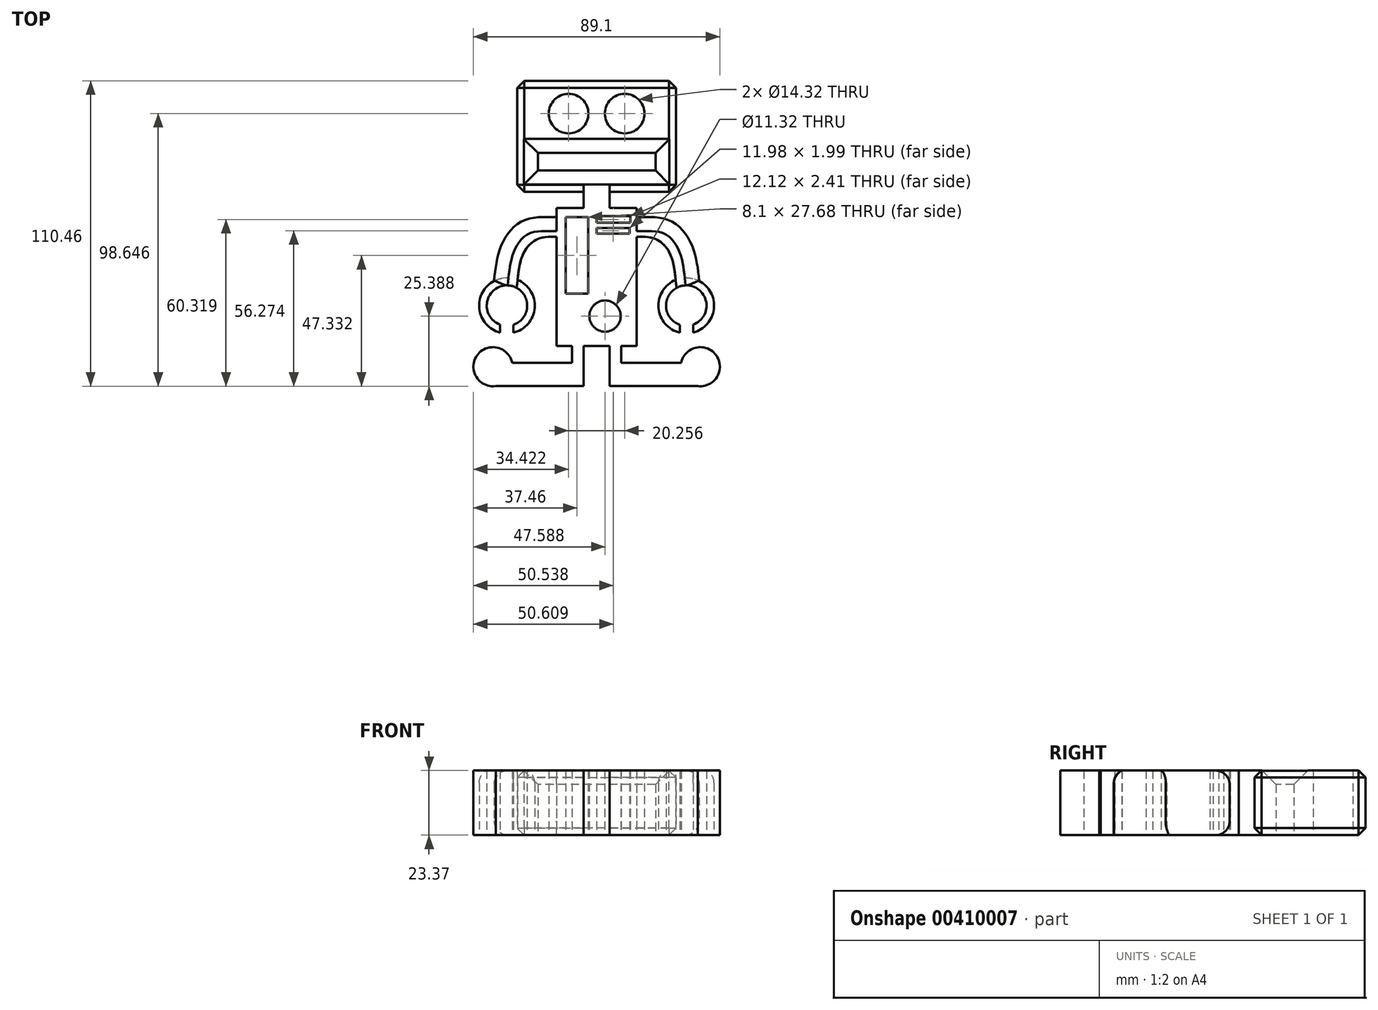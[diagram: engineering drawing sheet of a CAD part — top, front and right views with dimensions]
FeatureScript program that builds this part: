
annotation { "Feature Type Name" : "Feature", "Feature Type Description" : "" }
export const myFeature = defineFeature(function(context is Context, id is Id, definition is map)
    precondition{}
    {
        {
            var Q0;
            Q0=qCreatedBy(makeId("Top.planeOp"),FACE);
            var sketch = newSketch(context, id + "F0", { "sketchPlane" : qUnion([Q0])});
            skLineSegment(sketch, "E0.bottom", {"start": v(-28.7, 40.17) * mm, "end": v(0, 40.17) * mm});
            skLineSegment(sketch, "E0.left", {"start": v(-28.7, 40.17) * mm, "end": v(-28.7, 0) * mm});
            skLineSegment(sketch, "E1.MirrorCS", {"start": v(28.7, 40.17) * mm, "end": v(0, 40.17) * mm});
            skLineSegment(sketch, "E2.MirrorCS", {"start": v(28.7, 40.17) * mm, "end": v(28.7, 0) * mm});
            skCircle(sketch, "E3", {"center": v(-10.13, 28.36) * mm, "radius": 7.16 * mm});
            skLineSegment(sketch, "E4.bottom", {"start": v(-21.27, 14.18) * mm, "end": v(0, 14.18) * mm});
            skLineSegment(sketch, "E4.top", {"start": v(-21.27, 7.76) * mm, "end": v(0, 7.76) * mm});
            skLineSegment(sketch, "E4.left", {"start": v(-21.27, 14.18) * mm, "end": v(-21.27, 7.76) * mm});
            skLineSegment(sketch, "E5.MirrorCS", {"start": v(21.27, 14.18) * mm, "end": v(21.27, 7.76) * mm});
            skLineSegment(sketch, "E6.MirrorCS", {"start": v(21.27, 14.18) * mm, "end": v(0, 14.18) * mm});
            skLineSegment(sketch, "E7.MirrorCS", {"start": v(21.27, 7.76) * mm, "end": v(0, 7.76) * mm});
            skCircle(sketch, "E8.MirrorC", {"center": v(10.13, 28.36) * mm, "radius": 7.16 * mm});
            skLineSegment(sketch, "E9", {"start": v(-4.73, 0) * mm, "end": v(-4.73, -5.74) * mm});
            skLineSegment(sketch, "E10", {"start": v(-4.73, -5.74) * mm, "end": v(-14.52, -5.74) * mm});
            skLineSegment(sketch, "E11", {"start": v(-14.52, -5.74) * mm, "end": v(-14.52, -9.12) * mm});
            skLineSegment(sketch, "E12", {"start": v(-14.52, -55.7) * mm, "end": v(-8.9, -55.7) * mm});
            skFitSpline(sketch, "E13", {"points": [v(-14.52, -9.12) * mm, v(-26.67, -10.47) * mm, v(-34.43, -19.24) * mm, v(-37.14, -32.75) * mm], "startDerivative": vector(-39.34, 1.38) * mm, "endDerivative": vector(-4.09, -40.26) * mm});
            skFitSpline(sketch, "E14", {"points": [v(-14.52, -16.2) * mm, v(-20.93, -16.88) * mm, v(-26.33, -21.95) * mm, v(-28.7, -32.75) * mm], "startDerivative": vector(-22.24, 0.54) * mm, "endDerivative": vector(-3.26, -30.34) * mm});
            skArc(sketch, "E15", {"start": v(-37.08, -32.2) * mm, "mid": v(-42.4, -42.23) * mm, "end": v(-34.98, -50.83) * mm});
            skArc(sketch, "E16", {"start": v(-30.1, -48.04) * mm, "mid": v(-32.28, -33.79) * mm, "end": v(-34.98, -47.95) * mm});
            skLineSegment(sketch, "E17", {"start": v(-34.98, -47.95) * mm, "end": v(-34.98, -50.83) * mm});
            skLineSegment(sketch, "E18", {"start": v(-30.1, -48.04) * mm, "end": v(-30.1, -50.9) * mm});
            skArc(sketch, "E19.trimOffspring", {"start": v(-30.1, -50.9) * mm, "mid": v(-22.38, -41.9) * mm, "end": v(-28.6, -31.8) * mm});
            skLineSegment(sketch, "E20.bottom", {"start": v(-30.55, -61.78) * mm, "end": v(-8.9, -61.78) * mm});
            skLineSegment(sketch, "E20.top", {"start": v(-37.47, -70.22) * mm, "end": v(-4.73, -70.22) * mm});
            skLineSegment(sketch, "E20.right", {"start": v(-4.73, -61.78) * mm, "end": v(-4.73, -70.22) * mm});
            skLineSegment(sketch, "E21.left", {"start": v(-8.9, -55.7) * mm, "end": v(-8.9, -61.78) * mm});
            skLineSegment(sketch, "E21.right", {"start": v(-4.73, -55.7) * mm, "end": v(-4.73, -61.78) * mm});
            skLineSegment(sketch, "E22.trimOffspring", {"start": v(-4.73, -55.7) * mm, "end": v(0, -55.7) * mm});
            skLineSegment(sketch, "E23.trimOffspring", {"start": v(-14.52, -16.2) * mm, "end": v(-14.52, -55.7) * mm});
            skPoint(sketch, "E24.orphan", {"position": v(0, -5.74) * mm});
            skLineSegment(sketch, "E25.MirrorCS", {"start": v(14.52, -5.74) * mm, "end": v(14.52, -9.12) * mm});
            skLineSegment(sketch, "E26.MirrorCS", {"start": v(4.73, -55.7) * mm, "end": v(4.73, -61.78) * mm});
            skLineSegment(sketch, "E27.MirrorCS", {"start": v(30.1, -48.04) * mm, "end": v(30.1, -50.9) * mm});
            skLineSegment(sketch, "E28.MirrorCS", {"start": v(8.9, -55.7) * mm, "end": v(8.9, -61.78) * mm});
            skLineSegment(sketch, "E29.MirrorCS", {"start": v(4.73, -61.78) * mm, "end": v(4.73, -70.22) * mm});
            skLineSegment(sketch, "E30.MirrorCS", {"start": v(34.98, -47.95) * mm, "end": v(34.98, -50.83) * mm});
            skLineSegment(sketch, "E31.MirrorCS", {"start": v(14.52, -55.7) * mm, "end": v(8.9, -55.7) * mm});
            skLineSegment(sketch, "E32.MirrorCS", {"start": v(4.73, -55.7) * mm, "end": v(0, -55.7) * mm});
            skLineSegment(sketch, "E33.MirrorCS", {"start": v(4.73, 0) * mm, "end": v(4.73, -5.74) * mm});
            skFitSpline(sketch, "E34.MirrorCS", {"points": [v(14.52, -16.2) * mm, v(20.93, -16.88) * mm, v(26.33, -21.95) * mm, v(28.7, -32.75) * mm], "startDerivative": vector(22.24, 0.54) * mm, "endDerivative": vector(3.26, -30.34) * mm});
            skArc(sketch, "E35.MirrorCS", {"start": v(30.1, -50.9) * mm, "mid": v(22.38, -41.9) * mm, "end": v(28.6, -31.8) * mm});
            skFitSpline(sketch, "E36.MirrorCS", {"points": [v(14.52, -9.12) * mm, v(26.67, -10.47) * mm, v(34.43, -19.24) * mm, v(37.14, -32.75) * mm], "startDerivative": vector(39.34, 1.38) * mm, "endDerivative": vector(4.09, -40.26) * mm});
            skLineSegment(sketch, "E37.MirrorCS", {"start": v(14.52, -16.2) * mm, "end": v(14.52, -55.7) * mm});
            skArc(sketch, "E38.MirrorCS", {"start": v(37.08, -32.2) * mm, "mid": v(42.4, -42.23) * mm, "end": v(34.98, -50.83) * mm});
            skLineSegment(sketch, "E39.MirrorCS", {"start": v(37.47, -70.22) * mm, "end": v(4.73, -70.22) * mm});
            skArc(sketch, "E40.MirrorCS", {"start": v(30.1, -48.04) * mm, "mid": v(32.28, -33.79) * mm, "end": v(34.98, -47.95) * mm});
            skLineSegment(sketch, "E41.MirrorCS", {"start": v(30.55, -61.78) * mm, "end": v(8.9, -61.78) * mm});
            skLineSegment(sketch, "E42.MirrorCS", {"start": v(4.73, -5.74) * mm, "end": v(14.52, -5.74) * mm});
            skPoint(sketch, "E43.orphan", {"position": v(0, 0) * mm});
            skPoint(sketch, "E44.MirrorCS.start.orphan", {"position": v(28.7, 0) * mm});
            skLineSegment(sketch, "E45", {"start": v(-28.7, 0) * mm, "end": v(-4.73, 0) * mm});
            skLineSegment(sketch, "E46", {"start": v(4.73, 0) * mm, "end": v(28.7, 0) * mm});
            skArc(sketch, "E47", {"start": v(-30.55, -61.78) * mm, "mid": v(-43.25, -59.13) * mm, "end": v(-36.51, -70.22) * mm});
            skPoint(sketch, "E20.left.start.orphan", {"position": v(-37.47, -61.78) * mm});
            skArc(sketch, "E48.MirrorCS", {"start": v(30.55, -61.78) * mm, "mid": v(43.25, -59.13) * mm, "end": v(36.51, -70.22) * mm});
            skPoint(sketch, "E49.MirrorP", {"position": v(37.47, -61.78) * mm});
            skPoint(sketch, "E50.orphan", {"position": v(-37.47, -70.22) * mm});
            skLineSegment(sketch, "E51.bottom", {"start": v(-11.14, -9.12) * mm, "end": v(-3.04, -9.12) * mm});
            skLineSegment(sketch, "E51.top", {"start": v(-11.14, -36.8) * mm, "end": v(-3.04, -36.8) * mm});
            skLineSegment(sketch, "E51.left", {"start": v(-11.14, -9.12) * mm, "end": v(-11.14, -36.8) * mm});
            skLineSegment(sketch, "E51.right", {"start": v(-3.04, -9.12) * mm, "end": v(-3.04, -36.8) * mm});
            skLineSegment(sketch, "E52.bottom", {"start": v(0, -8.76) * mm, "end": v(12.12, -8.76) * mm});
            skLineSegment(sketch, "E52.top", {"start": v(0, -11.18) * mm, "end": v(12.12, -11.18) * mm});
            skLineSegment(sketch, "E52.left", {"start": v(0, -8.76) * mm, "end": v(0, -11.18) * mm});
            skLineSegment(sketch, "E52.right", {"start": v(12.12, -8.76) * mm, "end": v(12.12, -11.18) * mm});
            skLineSegment(sketch, "E53.bottom", {"start": v(0, -13.02) * mm, "end": v(11.98, -13.02) * mm});
            skLineSegment(sketch, "E53.top", {"start": v(0, -15) * mm, "end": v(11.98, -15) * mm});
            skLineSegment(sketch, "E53.left", {"start": v(0, -13.02) * mm, "end": v(0, -15) * mm});
            skLineSegment(sketch, "E53.right", {"start": v(11.98, -13.02) * mm, "end": v(11.98, -15) * mm});
            skCircle(sketch, "E54", {"center": v(3.04, -44.9) * mm, "radius": 5.66 * mm});
            skSolve(sketch);
        }
        {
            var Q0;
            Q0=makeQuery(id+"F0.imprint","IMPRINT",FACE,{"disambiguationData":[TD([[makeQuery(id+"F0.imprint","IMPRINT",EDGE,{"derivedFrom":sQuery(id+"F0.wireOp",EDGE,"E0.bottom")}),-1.0]])]});
            extrude(context, id + "F1", {"entities" : qUnion([Q0]), "depth" : 23.37 * mm});
        }
        {
            var Q0;
            Q0=makeQuery(id+"F1.opExtrude","CAP_EDGE",EDGE,{"disambiguationData":[OSD([sQuery(id+"F0.wireOp",EDGE,"E13")])],"isStart":false});
            var Q1;
            Q1=makeQuery(id+"F1.opExtrude","CAP_EDGE",EDGE,{"disambiguationData":[OSD([sQuery(id+"F0.wireOp",EDGE,"E36.MirrorCS")])],"isStart":false});
            var Q2;
            Q2=makeQuery(id+"F1.opExtrude","CAP_EDGE",EDGE,{"disambiguationData":[OSD([sQuery(id+"F0.wireOp",EDGE,"E13")])],"isStart":true});
            var Q3;
            Q3=makeQuery(id+"F1.opExtrude","CAP_EDGE",EDGE,{"disambiguationData":[OSD([sQuery(id+"F0.wireOp",EDGE,"E36.MirrorCS")])],"isStart":true});
            fillet(context, id + "F2", {"entities" : qUnion([Q0, Q1, Q2, Q3]), "radius" : 5.08 * mm, "tangentPropagation" : true, "allowEdgeOverflow" : false});
        }
        {
            var Q0;
            Q0=makeQuery(id+"F1.opExtrude","SWEPT_EDGE",EDGE,{"disambiguationData":[OSD([sQuery(id+"F0.wireOp",EDGE,"E0.bottom"),sQuery(id+"F0.wireOp",EDGE,"E0.left")])]});
            var Q1;
            Q1=makeQuery(id+"F1.opExtrude","CAP_EDGE",EDGE,{"disambiguationData":[OSD([sQuery(id+"F0.wireOp",EDGE,"E0.left")])],"isStart":false});
            var Q2;
            Q2=makeQuery(id+"F1.opExtrude","CAP_EDGE",EDGE,{"disambiguationData":[OSD([sQuery(id+"F0.wireOp",EDGE,"E0.bottom"),sQuery(id+"F0.wireOp",EDGE,"E1.MirrorCS")])],"isStart":false});
            var Q3;
            Q3=makeQuery(id+"F1.opExtrude","CAP_EDGE",EDGE,{"disambiguationData":[OSD([sQuery(id+"F0.wireOp",EDGE,"E2.MirrorCS")])],"isStart":false});
            var Q4;
            Q4=makeQuery(id+"F1.opExtrude","CAP_EDGE",EDGE,{"disambiguationData":[OSD([sQuery(id+"F0.wireOp",EDGE,"E46")])],"isStart":false});
            var Q5;
            Q5=makeQuery(id+"F1.opExtrude","CAP_EDGE",EDGE,{"disambiguationData":[OSD([sQuery(id+"F0.wireOp",EDGE,"E45")])],"isStart":false});
            var Q6;
            Q6=makeQuery(id+"F1.opExtrude","SWEPT_EDGE",EDGE,{"disambiguationData":[OSD([sQuery(id+"F0.wireOp",EDGE,"E2.MirrorCS"),sQuery(id+"F0.wireOp",EDGE,"E46")])]});
            var Q7;
            Q7=makeQuery(id+"F1.opExtrude","CAP_EDGE",EDGE,{"disambiguationData":[OSD([sQuery(id+"F0.wireOp",EDGE,"E0.bottom"),sQuery(id+"F0.wireOp",EDGE,"E1.MirrorCS")])],"isStart":true});
            var Q8;
            Q8=makeQuery(id+"F1.opExtrude","SWEPT_EDGE",EDGE,{"disambiguationData":[OSD([sQuery(id+"F0.wireOp",EDGE,"E1.MirrorCS"),sQuery(id+"F0.wireOp",EDGE,"E2.MirrorCS")])]});
            var Q9;
            Q9=makeQuery(id+"F1.opExtrude","CAP_EDGE",EDGE,{"disambiguationData":[OSD([sQuery(id+"F0.wireOp",EDGE,"E2.MirrorCS")])],"isStart":true});
            var Q10;
            Q10=makeQuery(id+"F1.opExtrude","CAP_EDGE",EDGE,{"disambiguationData":[OSD([sQuery(id+"F0.wireOp",EDGE,"E46")])],"isStart":true});
            var Q11;
            Q11=makeQuery(id+"F1.opExtrude","CAP_EDGE",EDGE,{"disambiguationData":[OSD([sQuery(id+"F0.wireOp",EDGE,"E45")])],"isStart":true});
            var Q12;
            Q12=makeQuery(id+"F1.opExtrude","CAP_EDGE",EDGE,{"disambiguationData":[OSD([sQuery(id+"F0.wireOp",EDGE,"E0.left")])],"isStart":true});
            var Q13;
            Q13=makeQuery(id+"F1.opExtrude","SWEPT_EDGE",EDGE,{"disambiguationData":[OSD([sQuery(id+"F0.wireOp",EDGE,"E0.left"),sQuery(id+"F0.wireOp",EDGE,"E45")])]});
            chamfer(context, id + "F3", {"entities" : qUnion([Q0, Q1, Q2, Q3, Q4, Q5, Q6, Q7, Q8, Q9, Q10, Q11, Q12, Q13]), "width" : 2.54 * mm, "tangentPropagation" : true});
        }
        {
            var Q0;
            Q0=makeQuery(id+"F1.opExtrude","CAP_EDGE",EDGE,{"disambiguationData":[OSD([sQuery(id+"F0.wireOp",EDGE,"E4.bottom"),sQuery(id+"F0.wireOp",EDGE,"E6.MirrorCS")])],"isStart":false});
            var Q1;
            Q1=makeQuery(id+"F1.opExtrude","CAP_EDGE",EDGE,{"disambiguationData":[OSD([sQuery(id+"F0.wireOp",EDGE,"E4.top"),sQuery(id+"F0.wireOp",EDGE,"E7.MirrorCS")])],"isStart":false});
            var Q2;
            Q2=makeQuery(id+"F1.opExtrude","CAP_EDGE",EDGE,{"disambiguationData":[OSD([sQuery(id+"F0.wireOp",EDGE,"E4.left")])],"isStart":false});
            var Q3;
            Q3=makeQuery(id+"F1.opExtrude","CAP_EDGE",EDGE,{"disambiguationData":[OSD([sQuery(id+"F0.wireOp",EDGE,"E5.MirrorCS")])],"isStart":false});
            chamfer(context, id + "F4", {"entities" : qUnion([Q0, Q1, Q2, Q3]), "width" : 5.08 * mm, "tangentPropagation" : true});
        }
        {
            var Q0;
            Q0=makeQuery(id+"F1.opExtrude","CAP_EDGE",EDGE,{"disambiguationData":[OSD([sQuery(id+"F0.wireOp",EDGE,"E15")])],"isStart":false});
            var Q1;
            Q1=makeQuery(id+"F1.opExtrude","CAP_EDGE",EDGE,{"disambiguationData":[OSD([sQuery(id+"F0.wireOp",EDGE,"E19.trimOffspring")])],"isStart":false});
            var Q2;
            Q2=makeQuery(id+"F1.opExtrude","CAP_EDGE",EDGE,{"disambiguationData":[OSD([sQuery(id+"F0.wireOp",EDGE,"E35.MirrorCS")])],"isStart":false});
            var Q3;
            Q3=makeQuery(id+"F1.opExtrude","CAP_EDGE",EDGE,{"disambiguationData":[OSD([sQuery(id+"F0.wireOp",EDGE,"E38.MirrorCS")])],"isStart":false});
            fillet(context, id + "F5", {"entities" : qUnion([Q0, Q1, Q2, Q3]), "radius" : 5.08 * mm, "tangentPropagation" : true, "allowEdgeOverflow" : false});
        }
    });
